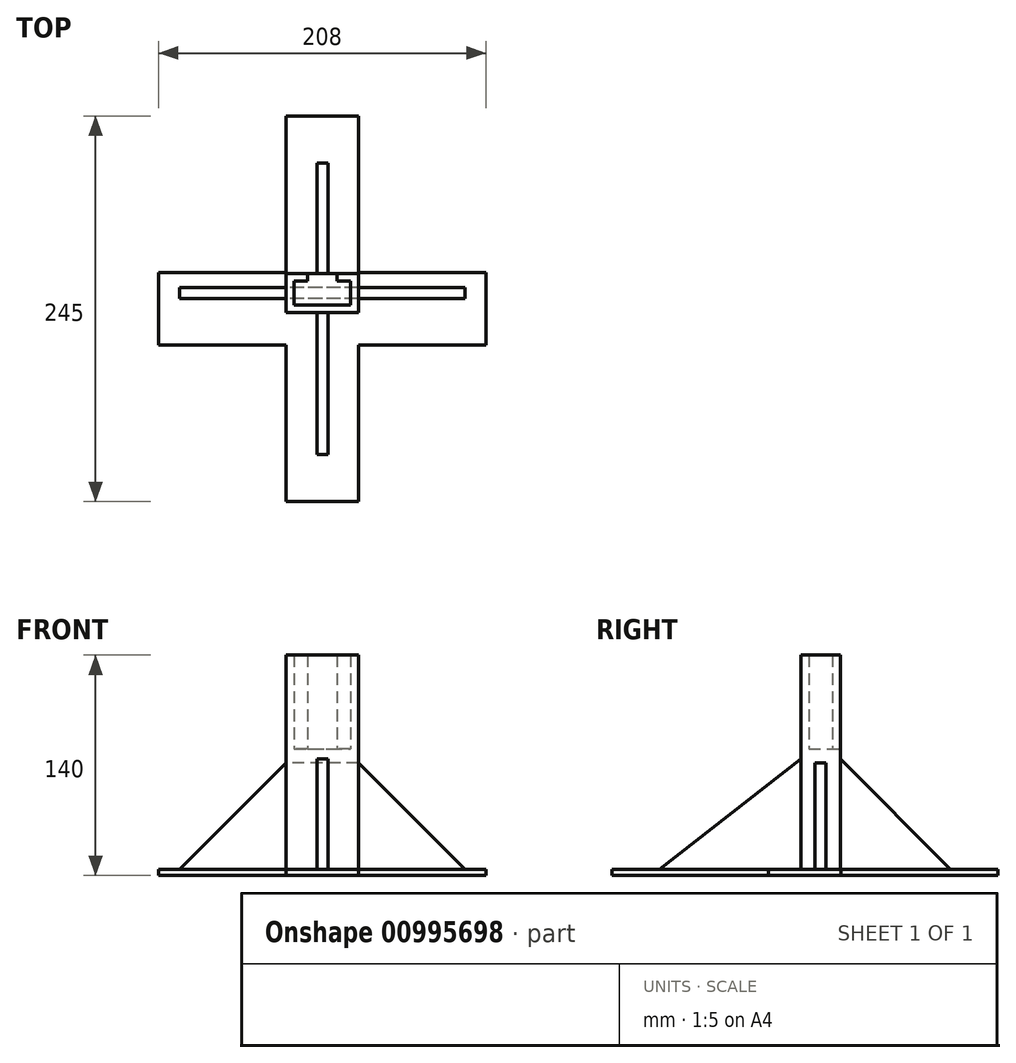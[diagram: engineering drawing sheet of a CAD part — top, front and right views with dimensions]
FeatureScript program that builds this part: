
annotation { "Feature Type Name" : "Feature", "Feature Type Description" : "" }
export const myFeature = defineFeature(function(context is Context, id is Id, definition is map)
    precondition{}
    {
        {
            var Q0;
            Q0=qCreatedBy(makeId("Front.planeOp"),FACE);
            var sketch = newSketch(context, id + "F0", { "sketchPlane" : qUnion([Q0])});
            skLineSegment(sketch, "E0.bottom", {"start": v(-35.47, 8.44) * mm, "end": v(10.53, 8.44) * mm});
            skLineSegment(sketch, "E0.top", {"start": v(-35.47, -71.56) * mm, "end": v(10.53, -71.56) * mm});
            skLineSegment(sketch, "E0.left", {"start": v(-35.47, 8.44) * mm, "end": v(-35.47, -71.56) * mm});
            skLineSegment(sketch, "E0.right", {"start": v(10.53, 8.44) * mm, "end": v(10.53, -71.56) * mm});
            skSolve(sketch);
        }
        {
            var Q0;
            Q0=makeQuery(id+"F0.imprint","IMPRINT",FACE,{"disambiguationData":[TD([[makeQuery(id+"F0.imprint","IMPRINT",EDGE,{"derivedFrom":sQuery(id+"F0.wireOp",EDGE,"E0.bottom")}),-1.0]])]});
            extrude(context, id + "F1", {"entities" : qUnion([Q0]), "depth" : 25 * mm, "offsetDistance" : 25 * mm});
        }
        {
            var Q0;
            Q0=makeQuery(id+"F1.opExtrude","SWEPT_FACE",FACE,{"disambiguationData":[OSD([sQuery(id+"F0.wireOp",EDGE,"E0.left")])]});
            var sketch = newSketch(context, id + "F2", { "sketchPlane" : qUnion([Q0])});
            skLineSegment(sketch, "E1", {"start": v(0, -71.56) * mm, "end": v(-100, -71.56) * mm});
            skLineSegment(sketch, "E2", {"start": v(-100, -71.56) * mm, "end": v(-100, -67.56) * mm});
            skLineSegment(sketch, "E3", {"start": v(-100, -67.56) * mm, "end": v(0, -67.56) * mm});
            skLineSegment(sketch, "E4", {"start": v(-70, -67.56) * mm, "end": v(0, 2.44) * mm});
            skLineSegment(sketch, "E5", {"start": v(25, -71.56) * mm, "end": v(145, -71.56) * mm});
            skLineSegment(sketch, "E6", {"start": v(145, -71.56) * mm, "end": v(145, -67.56) * mm});
            skLineSegment(sketch, "E7", {"start": v(145, -67.56) * mm, "end": v(25, -67.56) * mm});
            skLineSegment(sketch, "E8", {"start": v(25, 2.44) * mm, "end": v(115, -67.56) * mm});
            skPoint(sketch, "E9", {"position": v(-0.5, -71.56) * mm});
            skPoint(sketch, "E10", {"position": v(45.5, -71.56) * mm});
            skLineSegment(sketch, "E11", {"start": v(-0.5, -71.56) * mm, "end": v(-0.5, -67.56) * mm});
            skLineSegment(sketch, "E12", {"start": v(-0.5, -67.56) * mm, "end": v(45.5, -67.56) * mm});
            skLineSegment(sketch, "E13", {"start": v(45.5, -67.56) * mm, "end": v(45.5, -71.56) * mm});
            skSolve(sketch);
        }
        {
            var Q0;
            Q0=makeQuery(id+"F1.opExtrude","SWEPT_FACE",FACE,{"disambiguationData":[OSD([sQuery(id+"F0.wireOp",EDGE,"E0.bottom")])]});
            var sketch = newSketch(context, id + "F3", { "sketchPlane" : qUnion([Q0])});
            skLineSegment(sketch, "E14.0.0", {"start": v(10.53, 0) * mm, "end": v(-35.47, 0) * mm});
            skLineSegment(sketch, "E14.0.1", {"start": v(-35.47, 0) * mm, "end": v(-35.47, -25) * mm});
            skLineSegment(sketch, "E14.0.2", {"start": v(-35.47, -25) * mm, "end": v(10.53, -25) * mm});
            skLineSegment(sketch, "E14.0.3", {"start": v(10.53, -25) * mm, "end": v(10.53, 0) * mm});
            skLineSegment(sketch, "E15.0", {"start": v(5.53, -5) * mm, "end": v(-30.47, -5) * mm});
            skLineSegment(sketch, "E15.1", {"start": v(5.53, -20) * mm, "end": v(5.53, -5) * mm});
            skLineSegment(sketch, "E15.2", {"start": v(-30.47, -20) * mm, "end": v(5.53, -20) * mm});
            skLineSegment(sketch, "E15.3", {"start": v(-30.47, -5) * mm, "end": v(-30.47, -20) * mm});
            skPoint(sketch, "E16", {"position": v(-21.72, -5) * mm});
            skPoint(sketch, "E17", {"position": v(-3.22, -5) * mm});
            skLineSegment(sketch, "E18", {"start": v(-21.72, -5) * mm, "end": v(-21.72, 0) * mm});
            skLineSegment(sketch, "E19", {"start": v(-3.22, -5) * mm, "end": v(-3.22, 0) * mm});
            skPoint(sketch, "E20", {"position": v(-12.47, -5) * mm});
            skSolve(sketch);
        }
        {
            var Q0;
            {var subQ6=sQuery(id+"F3.wireOp",EDGE,"E14.0.1");Q0=makeQuery(id+"F3.imprint","IMPRINT",FACE,{"disambiguationData":[TD([[makeQuery(id+"F3.imprint","IMPRINT",EDGE,{"derivedFrom":subQ6}),-1.0]])]});}
            extrude(context, id + "F4", {"entities" : qUnion([Q0]), "operationType" : NewBodyOperationType.ADD, "depth" : 60 * mm, "offsetDistance" : 25 * mm});
        }
        {
            var Q0;
            {var subQ4=sQuery(id+"F2.wireOp",EDGE,"E11");Q0=makeQuery(id+"F2.imprint","IMPRINT",FACE,{"disambiguationData":[TD([[makeQuery(id+"F2.imprint","IMPRINT",EDGE,{"derivedFrom":subQ4}),-1.0]])]});}
            var Q1;
            {var subQ4=sQuery(id+"F2.wireOp",EDGE,"E13");Q1=makeQuery(id+"F2.imprint","IMPRINT",FACE,{"disambiguationData":[TD([[makeQuery(id+"F2.imprint","IMPRINT",EDGE,{"derivedFrom":subQ4}),-1.0]])]});}
            var Q2;
            {var subQ1=sQuery(id+"F2.wireOp",EDGE,"E2");Q2=makeQuery(id+"F2.imprint","IMPRINT",FACE,{"disambiguationData":[TD([[makeQuery(id+"F2.imprint","IMPRINT",EDGE,{"derivedFrom":subQ1}),-1.0]])]});}
            var Q3;
            {var subQ1=sQuery(id+"F2.wireOp",EDGE,"E6");Q3=makeQuery(id+"F2.imprint","IMPRINT",FACE,{"disambiguationData":[TD([[makeQuery(id+"F2.imprint","IMPRINT",EDGE,{"derivedFrom":subQ1}),1.0]])]});}
            extrude(context, id + "F5", {"entities" : qUnion([Q0, Q1, Q2, Q3]), "operationType" : NewBodyOperationType.ADD, "oppositeDirection" : true, "depth" : 46 * mm, "offsetDistance" : 25 * mm});
        }
        {
            var Q0;
            {var subQ0=sQuery(id+"F0.wireOp",EDGE,"E0.left");Q0=makeQuery(id+"F5.boolean.opBoolean","MERGE",FACE,{"derivedFrom":[makeQuery(id+"F4.boolean.opBoolean","MERGE",FACE,{"derivedFrom":[makeQuery(id+"F1.opExtrude","SWEPT_FACE",FACE,{"disambiguationData":[OSD([subQ0])]}),makeQuery(id+"F4.opExtrude","SWEPT_FACE",FACE,{"disambiguationData":[OSD([sQuery(id+"F3.wireOp",EDGE,"E14.0.1")])]})]}),makeQuery(id+"F5.opExtrude","CAP_FACE",FACE,{"disambiguationData":[OSD([subQ0,sQuery(id+"F2.wireOp",EDGE,"E1"),sQuery(id+"F2.wireOp",EDGE,"E2"),sQuery(id+"F2.wireOp",EDGE,"E3")])],"isStart":true}),makeQuery(id+"F5.opExtrude","CAP_FACE",FACE,{"disambiguationData":[OSD([subQ0,sQuery(id+"F2.wireOp",EDGE,"E5"),sQuery(id+"F2.wireOp",EDGE,"E6"),sQuery(id+"F2.wireOp",EDGE,"E7")])],"isStart":true})]});}
            cPlane(context, id + "F6", {"entities" : qUnion([Q0]), "cplaneType" : CPlaneType.OFFSET, "offset" : 23 * mm, "oppositeDirection" : true, "width" : 150 * mm, "height" : 150 * mm});
        }
        {
            var Q0;
            Q0=qCreatedBy(id+"F6.planeOp",FACE);
            var sketch = newSketch(context, id + "F7", { "sketchPlane" : qUnion([Q0])});
            skLineSegment(sketch, "E21.0.0", {"start": v(0, 68.44) * mm, "end": v(0, -67.56) * mm});
            skLineSegment(sketch, "E21.0.2", {"start": v(0, -67.56) * mm, "end": v(0, 68.44) * mm});
            skLineSegment(sketch, "E21.0.4", {"start": v(0, 68.44) * mm, "end": v(0, 8.44) * mm});
            skLineSegment(sketch, "E21.0.6", {"start": v(0, 8.44) * mm, "end": v(0, 68.44) * mm});
            skLineSegment(sketch, "E22", {"start": v(0, -67.56) * mm, "end": v(-70, -67.56) * mm});
            skLineSegment(sketch, "E23", {"start": v(-70, -67.56) * mm, "end": v(0, 2.44) * mm});
            skLineSegment(sketch, "E24.0.1", {"start": v(25, -67.56) * mm, "end": v(25, 68.44) * mm});
            skLineSegment(sketch, "E24.0.3", {"start": v(25, 68.44) * mm, "end": v(25, -67.56) * mm});
            skLineSegment(sketch, "E25", {"start": v(25, -67.56) * mm, "end": v(115, -67.56) * mm});
            skLineSegment(sketch, "E26", {"start": v(115, -67.56) * mm, "end": v(25, 2.44) * mm});
            skSolve(sketch);
        }
        {
            var Q0;
            {var subQ0=sQuery(id+"F7.wireOp",EDGE,"E22");Q0=makeQuery(id+"F7.imprint","IMPRINT",FACE,{"disambiguationData":[TD([[makeQuery(id+"F7.imprint","IMPRINT",EDGE,{"derivedFrom":subQ0}),-1.0]])]});}
            var Q1;
            {var subQ0=sQuery(id+"F7.wireOp",EDGE,"E25");Q1=makeQuery(id+"F7.imprint","IMPRINT",FACE,{"disambiguationData":[TD([[makeQuery(id+"F7.imprint","IMPRINT",EDGE,{"derivedFrom":subQ0}),1.0]])]});}
            extrude(context, id + "F8", {"entities" : qUnion([Q0, Q1]), "operationType" : NewBodyOperationType.ADD, "endBound" : BoundingType.SYMMETRIC, "depth" : 7 * mm, "offsetDistance" : 25 * mm});
        }
        {
            var Q0;
            {var subQ0=sQuery(id+"F3.wireOp",EDGE,"E14.0.0");Q0=makeQuery(id+"F4.boolean.opBoolean","MERGE",FACE,{"derivedFrom":[makeQuery(id+"F1.opExtrude","CAP_FACE",FACE,{"disambiguationData":[OSD([sQuery(id+"F0.wireOp",EDGE,"E0.bottom"),sQuery(id+"F0.wireOp",EDGE,"E0.top"),sQuery(id+"F0.wireOp",EDGE,"E0.left"),sQuery(id+"F0.wireOp",EDGE,"E0.right")])],"isStart":true}),makeQuery(id+"F4.opExtrude","SWEPT_FACE",FACE,{"disambiguationData":[OSD([subQ0]),TDD([makeQuery(id+"F3.imprint","IMPRINT",EDGE,{"disambiguationData":[TD([[makeQuery(id+"F3.imprint","INTERSECT",VERTEX,{"derivedFrom":[subQ0,sQuery(id+"F3.wireOp",EDGE,"E14.0.1")]}),-1.0]])],"derivedFrom":subQ0})])]}),makeQuery(id+"F4.opExtrude","SWEPT_FACE",FACE,{"disambiguationData":[OSD([subQ0]),TDD([makeQuery(id+"F3.imprint","IMPRINT",EDGE,{"disambiguationData":[TD([[makeQuery(id+"F3.imprint","INTERSECT",VERTEX,{"derivedFrom":[subQ0,sQuery(id+"F3.wireOp",EDGE,"E14.0.3")]}),1.0]])],"derivedFrom":subQ0})])]})]});}
            var sketch = newSketch(context, id + "F9", { "sketchPlane" : qUnion([Q0])});
            skLineSegment(sketch, "E27", {"start": v(21.72, 8.84) * mm, "end": v(21.72, -71.56) * mm});
            skSolve(sketch);
        }
        {
            var Q0;
            Q0=makeQuery(id+"F1.opExtrude","SWEPT_FACE",FACE,{"disambiguationData":[OSD([sQuery(id+"F0.wireOp",EDGE,"E0.bottom")])]});
            var Q1;
            Q1=sQuery(id+"F9.wireOp",VERTEX,"E27.start");
            extrude(context, id + "F10", {"entities" : qUnion([Q0]), "operationType" : NewBodyOperationType.ADD, "endBound" : BoundingType.UP_TO_VERTEX, "depth" : 2.2 * mm, "endBoundEntityVertex" : qUnion([Q1]), "offsetDistance" : 25 * mm});
        }
        {
            var Q0;
            {var subQ4=sQuery(id+"F2.wireOp",EDGE,"E11");Q0=makeQuery(id+"F2.imprint","IMPRINT",FACE,{"disambiguationData":[TD([[makeQuery(id+"F2.imprint","IMPRINT",EDGE,{"derivedFrom":subQ4}),-1.0]])]});}
            var Q1;
            {var subQ0=sQuery(id+"F2.wireOp",EDGE,"E12");Q1=makeQuery(id+"F2.imprint","IMPRINT",FACE,{"disambiguationData":[TD([[makeQuery(id+"F2.imprint","IMPRINT",EDGE,{"derivedFrom":subQ0}),-1.0]])]});}
            var Q2;
            {var subQ4=sQuery(id+"F2.wireOp",EDGE,"E13");Q2=makeQuery(id+"F2.imprint","IMPRINT",FACE,{"disambiguationData":[TD([[makeQuery(id+"F2.imprint","IMPRINT",EDGE,{"derivedFrom":subQ4}),-1.0]])]});}
            extrude(context, id + "F11", {"entities" : qUnion([Q0, Q1, Q2]), "operationType" : NewBodyOperationType.ADD, "depth" : 81 * mm, "offsetDistance" : 25 * mm, "hasSecondDirection" : true, "secondDirectionOppositeDirection" : true, "secondDirectionDepth" : 127 * mm});
        }
        {
            var Q0;
            {var subQ0=sQuery(id+"F0.wireOp",EDGE,"E0.bottom");var subQ1=sQuery(id+"F3.wireOp",EDGE,"E14.0.0");Q0=makeQuery(id+"F10.boolean.opBoolean","MERGE",FACE,{"derivedFrom":[makeQuery(id+"F4.boolean.opBoolean","MERGE",FACE,{"derivedFrom":[makeQuery(id+"F1.opExtrude","CAP_FACE",FACE,{"disambiguationData":[OSD([subQ0,sQuery(id+"F0.wireOp",EDGE,"E0.top"),sQuery(id+"F0.wireOp",EDGE,"E0.left"),sQuery(id+"F0.wireOp",EDGE,"E0.right")])],"isStart":true}),makeQuery(id+"F4.opExtrude","SWEPT_FACE",FACE,{"disambiguationData":[OSD([subQ1]),TDD([makeQuery(id+"F3.imprint","IMPRINT",EDGE,{"disambiguationData":[TD([[makeQuery(id+"F3.imprint","INTERSECT",VERTEX,{"derivedFrom":[subQ1,sQuery(id+"F3.wireOp",EDGE,"E14.0.1")]}),-1.0]])],"derivedFrom":subQ1})])]}),makeQuery(id+"F4.opExtrude","SWEPT_FACE",FACE,{"disambiguationData":[OSD([subQ1]),TDD([makeQuery(id+"F3.imprint","IMPRINT",EDGE,{"disambiguationData":[TD([[makeQuery(id+"F3.imprint","INTERSECT",VERTEX,{"derivedFrom":[subQ1,sQuery(id+"F3.wireOp",EDGE,"E14.0.3")]}),1.0]])],"derivedFrom":subQ1})])]})]}),makeQuery(id+"F10.opExtrude","SWEPT_FACE",FACE,{"disambiguationData":[OSD([subQ0])]})]});}
            cPlane(context, id + "F12", {"entities" : qUnion([Q0]), "cplaneType" : CPlaneType.OFFSET, "offset" : 12.5 * mm, "oppositeDirection" : true, "width" : 150 * mm, "height" : 150 * mm});
        }
        {
            var Q0;
            Q0=qCreatedBy(id+"F12.planeOp",FACE);
            var sketch = newSketch(context, id + "F13", { "sketchPlane" : qUnion([Q0])});
            skLineSegment(sketch, "E28", {"start": v(35.47, 0) * mm, "end": v(103.02, -67.56) * mm});
            skLineSegment(sketch, "E29", {"start": v(-10.53, 0) * mm, "end": v(-78.09, -67.56) * mm});
            skLineSegment(sketch, "E30", {"start": v(-78.09, -67.56) * mm, "end": v(103.02, -67.56) * mm});
            skLineSegment(sketch, "E31", {"start": v(-10.53, 0) * mm, "end": v(35.47, 0) * mm});
            skSolve(sketch);
        }
        {
            var Q0;
            Q0 = qSketchRegion(id + "F13", true);
            extrude(context, id + "F14", {"entities" : qUnion([Q0]), "endBound" : BoundingType.SYMMETRIC, "depth" : 7 * mm, "offsetDistance" : 25 * mm});
        }
    });
